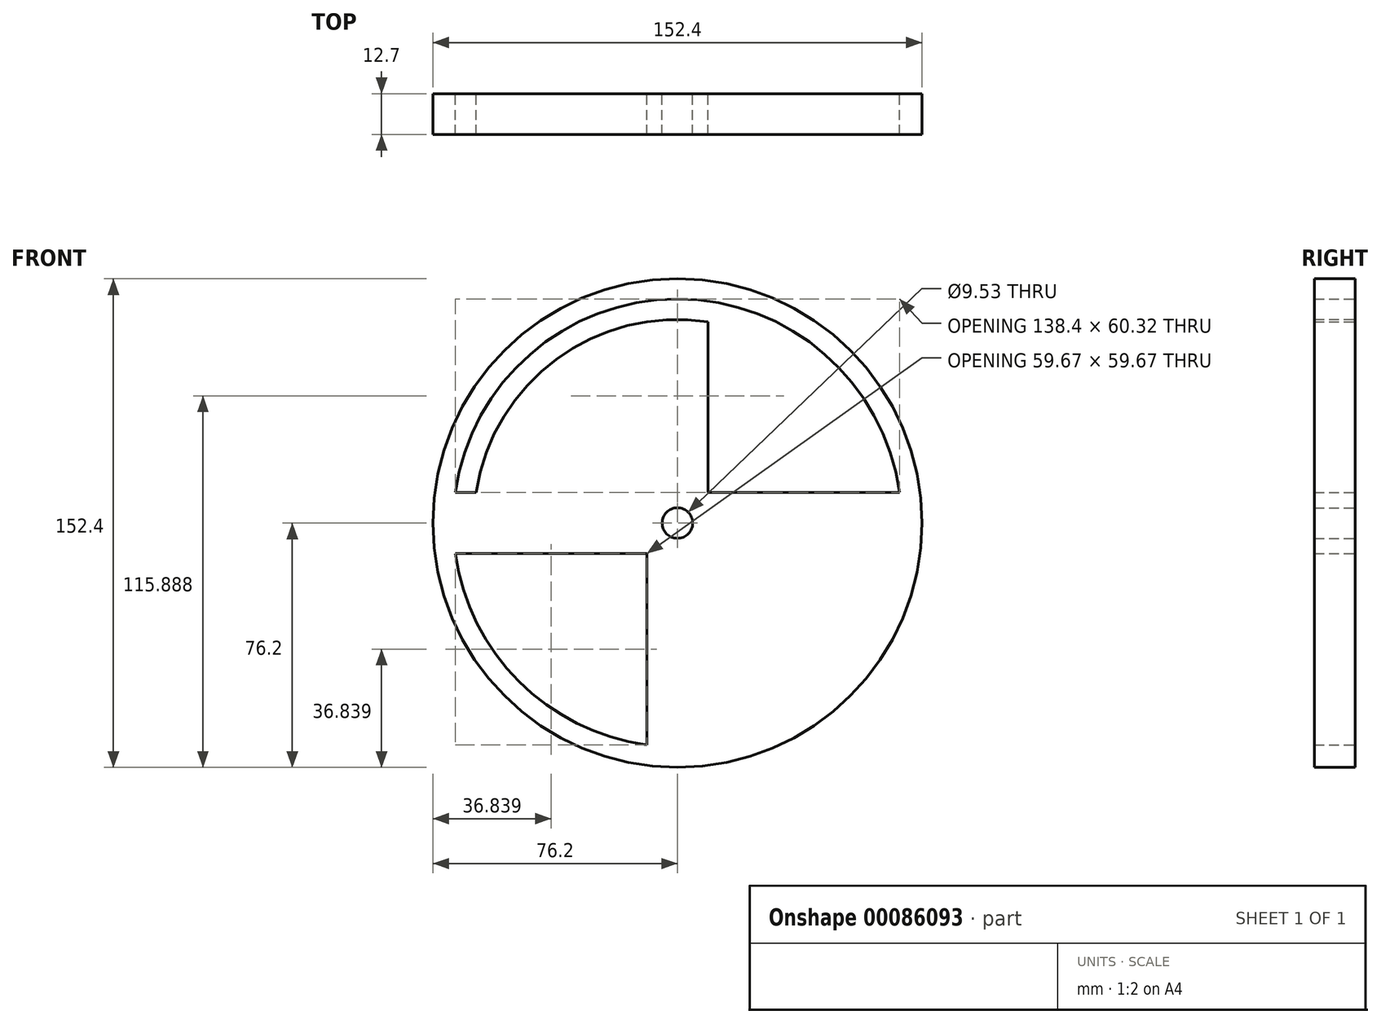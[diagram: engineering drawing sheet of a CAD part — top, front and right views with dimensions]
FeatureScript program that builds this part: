
annotation { "Feature Type Name" : "Feature", "Feature Type Description" : "" }
export const myFeature = defineFeature(function(context is Context, id is Id, definition is map)
    precondition{}
    {
        {
            var Q0;
            Q0=qCreatedBy(makeId("Front.planeOp"),FACE);
            var sketch = newSketch(context, id + "F0", { "sketchPlane" : qUnion([Q0])});
            skCircle(sketch, "E0", {"center": v(0, 0) * mm, "radius": 76.2 * mm});
            skCircle(sketch, "E1", {"center": v(0, 0) * mm, "radius": 63.5 * mm});
            skLineSegment(sketch, "E2", {"start": v(0, 76.2) * mm, "end": v(0, -76.2) * mm, "construction": true});
            skLineSegment(sketch, "E3", {"start": v(76.2, 0) * mm, "end": v(-76.2, 0) * mm, "construction": true});
            skLineSegment(sketch, "E4", {"start": v(-9.53, 75.6) * mm, "end": v(-9.52, -75.6) * mm});
            skLineSegment(sketch, "E5.MirrorCS", {"start": v(9.53, 75.6) * mm, "end": v(9.53, -75.6) * mm});
            skLineSegment(sketch, "E6", {"start": v(-75.6, 9.52) * mm, "end": v(75.6, 9.53) * mm});
            skLineSegment(sketch, "E7.MirrorCS", {"start": v(-75.6, -9.52) * mm, "end": v(75.6, -9.53) * mm});
            skCircle(sketch, "E8", {"center": v(0, 0) * mm, "radius": 4.76 * mm});
            skCircle(sketch, "E9", {"center": v(0, 0) * mm, "radius": 69.85 * mm});
            skSolve(sketch);
        }
        {
            var Q0;
            Q0 = qSketchRegion(id + "F0", true);
            var Q1;
            {var subQ0=sQuery(id+"F0.wireOp",EDGE,"E4");var subQ1=sQuery(id+"F0.wireOp",EDGE,"E1");var subQ2=makeQuery(id+"F0.imprint","INTERSECT",VERTEX,{"disambiguationData":[OD(0.0)],"derivedFrom":[subQ1,subQ0]});Q1=makeQuery(id+"F0.imprint","IMPRINT",FACE,{"disambiguationData":[TD([[makeQuery(id+"F0.imprint","IMPRINT",EDGE,{"disambiguationData":[TD([[subQ2,-1.0]])],"derivedFrom":subQ1}),1.0]])]});}
            var Q2;
            {var subQ0=sQuery(id+"F0.wireOp",EDGE,"E5.MirrorCS");var subQ1=sQuery(id+"F0.wireOp",EDGE,"E1");var subQ2=makeQuery(id+"F0.imprint","INTERSECT",VERTEX,{"disambiguationData":[OD(0.0)],"derivedFrom":[subQ1,subQ0]});Q2=makeQuery(id+"F0.imprint","IMPRINT",FACE,{"disambiguationData":[TD([[makeQuery(id+"F0.imprint","IMPRINT",EDGE,{"disambiguationData":[TD([[subQ2,1.0]])],"derivedFrom":subQ1}),1.0]])]});}
            var Q3;
            {var subQ0=sQuery(id+"F0.wireOp",EDGE,"E5.MirrorCS");var subQ1=sQuery(id+"F0.wireOp",EDGE,"E1");var subQ2=makeQuery(id+"F0.imprint","INTERSECT",VERTEX,{"disambiguationData":[OD(1.0)],"derivedFrom":[subQ1,subQ0]});Q3=makeQuery(id+"F0.imprint","IMPRINT",FACE,{"disambiguationData":[TD([[makeQuery(id+"F0.imprint","IMPRINT",EDGE,{"disambiguationData":[TD([[subQ2,-1.0]])],"derivedFrom":subQ1}),1.0]])]});}
            var Q4;
            {var subQ0=sQuery(id+"F0.wireOp",EDGE,"E7.MirrorCS");var subQ1=sQuery(id+"F0.wireOp",EDGE,"E1");var subQ2=makeQuery(id+"F0.imprint","INTERSECT",VERTEX,{"disambiguationData":[OD(0.0)],"derivedFrom":[subQ1,subQ0]});Q4=makeQuery(id+"F0.imprint","IMPRINT",FACE,{"disambiguationData":[TD([[makeQuery(id+"F0.imprint","IMPRINT",EDGE,{"disambiguationData":[TD([[subQ2,-1.0]])],"derivedFrom":subQ1}),1.0]])]});}
            var Q5;
            {var subQ0=sQuery(id+"F0.wireOp",EDGE,"E6");var subQ1=sQuery(id+"F0.wireOp",EDGE,"E1");var subQ2=makeQuery(id+"F0.imprint","INTERSECT",VERTEX,{"disambiguationData":[OD(1.0)],"derivedFrom":[subQ1,subQ0]});Q5=makeQuery(id+"F0.imprint","IMPRINT",FACE,{"disambiguationData":[TD([[makeQuery(id+"F0.imprint","IMPRINT",EDGE,{"disambiguationData":[TD([[subQ2,-1.0]])],"derivedFrom":subQ1}),1.0]])]});}
            var Q6;
            {var subQ0=sQuery(id+"F0.wireOp",EDGE,"E6");var subQ1=sQuery(id+"F0.wireOp",EDGE,"E1");var subQ2=makeQuery(id+"F0.imprint","INTERSECT",VERTEX,{"disambiguationData":[OD(0.0)],"derivedFrom":[subQ1,subQ0]});Q6=makeQuery(id+"F0.imprint","IMPRINT",FACE,{"disambiguationData":[TD([[makeQuery(id+"F0.imprint","IMPRINT",EDGE,{"disambiguationData":[TD([[subQ2,1.0]])],"derivedFrom":subQ1}),1.0]])]});}
            var Q7;
            {var subQ0=sQuery(id+"F0.wireOp",EDGE,"E5.MirrorCS");var subQ1=sQuery(id+"F0.wireOp",EDGE,"E1");var subQ2=makeQuery(id+"F0.imprint","INTERSECT",VERTEX,{"disambiguationData":[OD(0.0)],"derivedFrom":[subQ1,subQ0]});Q7=makeQuery(id+"F0.imprint","IMPRINT",FACE,{"disambiguationData":[TD([[makeQuery(id+"F0.imprint","IMPRINT",EDGE,{"disambiguationData":[TD([[subQ2,-1.0]])],"derivedFrom":subQ1}),1.0]])]});}
            var Q8;
            {var subQ0=sQuery(id+"F0.wireOp",EDGE,"E4");var subQ1=sQuery(id+"F0.wireOp",EDGE,"E1");var subQ2=makeQuery(id+"F0.imprint","INTERSECT",VERTEX,{"disambiguationData":[OD(1.0)],"derivedFrom":[subQ1,subQ0]});Q8=makeQuery(id+"F0.imprint","IMPRINT",FACE,{"disambiguationData":[TD([[makeQuery(id+"F0.imprint","IMPRINT",EDGE,{"disambiguationData":[TD([[subQ2,-1.0]])],"derivedFrom":subQ1}),1.0]])]});}
            var Q9;
            Q9=makeQuery(id+"F0.imprint","IMPRINT",FACE,{"disambiguationData":[TD([[makeQuery(id+"F0.imprint","IMPRINT",EDGE,{"derivedFrom":sQuery(id+"F0.wireOp",EDGE,"E8")}),-1.0]])]});
            var Q10;
            {var subQ0=sQuery(id+"F0.wireOp",EDGE,"E5.MirrorCS");var subQ1=sQuery(id+"F0.wireOp",EDGE,"E1");var subQ2=makeQuery(id+"F0.imprint","INTERSECT",VERTEX,{"disambiguationData":[OD(0.0)],"derivedFrom":[subQ1,subQ0]});Q10=makeQuery(id+"F0.imprint","IMPRINT",FACE,{"disambiguationData":[TD([[makeQuery(id+"F0.imprint","IMPRINT",EDGE,{"disambiguationData":[TD([[subQ2,-1.0]])],"derivedFrom":subQ1}),-1.0]])]});}
            var Q11;
            {var subQ0=sQuery(id+"F0.wireOp",EDGE,"E6");var subQ1=sQuery(id+"F0.wireOp",EDGE,"E1");var subQ2=makeQuery(id+"F0.imprint","INTERSECT",VERTEX,{"disambiguationData":[OD(1.0)],"derivedFrom":[subQ1,subQ0]});Q11=makeQuery(id+"F0.imprint","IMPRINT",FACE,{"disambiguationData":[TD([[makeQuery(id+"F0.imprint","IMPRINT",EDGE,{"disambiguationData":[TD([[subQ2,-1.0]])],"derivedFrom":subQ1}),-1.0]])]});}
            var Q12;
            {var subQ0=sQuery(id+"F0.wireOp",EDGE,"E4");var subQ1=sQuery(id+"F0.wireOp",EDGE,"E1");var subQ2=makeQuery(id+"F0.imprint","INTERSECT",VERTEX,{"disambiguationData":[OD(1.0)],"derivedFrom":[subQ1,subQ0]});Q12=makeQuery(id+"F0.imprint","IMPRINT",FACE,{"disambiguationData":[TD([[makeQuery(id+"F0.imprint","IMPRINT",EDGE,{"disambiguationData":[TD([[subQ2,-1.0]])],"derivedFrom":subQ1}),-1.0]])]});}
            var Q13;
            {var subQ0=sQuery(id+"F0.wireOp",EDGE,"E6");var subQ1=sQuery(id+"F0.wireOp",EDGE,"E1");var subQ2=makeQuery(id+"F0.imprint","INTERSECT",VERTEX,{"disambiguationData":[OD(0.0)],"derivedFrom":[subQ1,subQ0]});Q13=makeQuery(id+"F0.imprint","IMPRINT",FACE,{"disambiguationData":[TD([[makeQuery(id+"F0.imprint","IMPRINT",EDGE,{"disambiguationData":[TD([[subQ2,1.0]])],"derivedFrom":subQ1}),-1.0]])]});}
            extrude(context, id + "F1", {"entities" : qUnion([Q0, Q1, Q2, Q3, Q4, Q5, Q6, Q7, Q8, Q9, Q10, Q11, Q12, Q13]), "depth" : 12.7 * mm});
        }
    });
